# Revit family: Stirnplatte 35-21, VA
name_source: partatom
category: HLS-Bauteile
revit_build: Autodesk Revit 2017 (Build: 20190507_1515(x64)
units: mm (PartAtom-declared; Revit-internal decimal feet)

## family parameters
Basisbauteil = Fläche
Beim Laden mit Abzugskörper schneiden = Nein
Bemaßung runder Anschluss = Durchmesser verwenden
Gemeinsam genutzt = Ja
Raumberechnungspunkt = Nein
Teiletyp = Normal

## types (1)
- Stirnplatte 35-21, V2A
    Artikelnummer = 0480660
    Ausrichtung Platte = längs
    Befestigung = Montageschiene
    Breite Platte = 35 mm  [stored 0.114829 ft]
    EAN = 4250928412836
    Fabrikat = MEFA
    Firma = MEFA Befestigungs- und Montagesysteme GmbH
    Gewicht = 0.30 kg
    Gewicht pro Bauteil = 0.30 kg
    Kurztext1 = Stirnplatte C-Profil 35 längs V2A
    Kurztext2 = für C-Profil 35/21
    Lochabstand = 85 mm
    Lochdurchmesser = 13 mm
    Länge = 0 mm  [stored 0 ft]
    Länge Platte = 115 mm  [stored 0.377297 ft]
    Material = Edelstahl
    Profil = C-Profil
    Profilname = 35/21
    Profiltyp = 35/21
    Sicherheitsfaktor = 0
    Stärke Platte = 4 mm  [stored 0.0131234 ft]
    Vorgabe-Ansicht = 1219 mm
    max. Profilhöhe = 21 mm  [stored 0.0688976 ft]
    max. zul. Last Druck = 0.00 kip

note: [stored X ft] marks values corroborated as IEEE doubles in the binary element streams (Revit-internal decimal feet)
